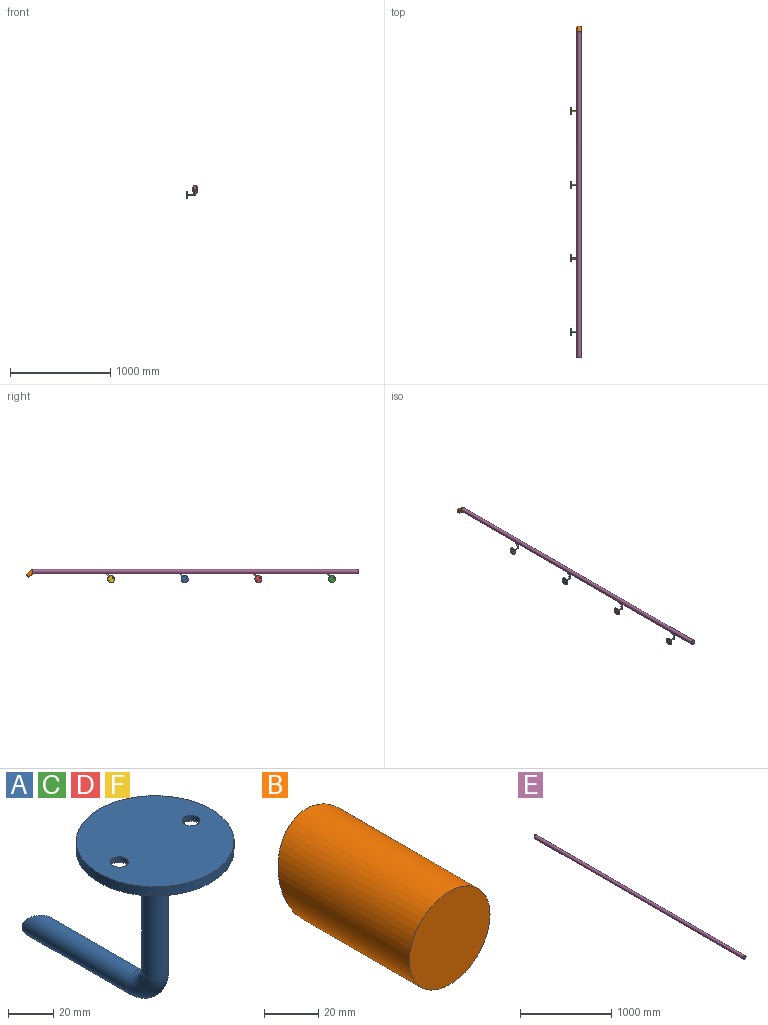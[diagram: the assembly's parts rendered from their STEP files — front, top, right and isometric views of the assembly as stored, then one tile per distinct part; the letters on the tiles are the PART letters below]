
ASSEMBLY  parts=6 mates=5
PART A: 11 faces, bbox 72.1x114.6x92.1 mm
  f0: cylinder r=6mm len=65.53mm, axis (0,-1,0), area 2289.2mm2, adj f1,f10
  f1: torus R=12mm, axis (-1,0,0), area 710.6mm2, adj f0,f2
  f2: cylinder r=6mm len=65.5mm, axis (0,0,1), area 2469.3mm2, adj f1,f5
  f3: cylinder r=35mm len=70mm, axis (0,0,-1), area 1099.6mm2, adj f4,f5
  f4: plane 70x70mm, normal (0,0,1), area 3747.9mm2, adj f3,f6,f7
  f5: plane 70x70mm, normal (0,0,-1), area 3469.9mm2, adj f2,f3,f8,f9
  f6: cylinder r=4mm len=8mm, axis (0,0,-1), area 62.8mm2, adj f4,f9
  f7: cylinder r=4mm len=8mm, axis (0,0,-1), area 62.8mm2, adj f4,f8
  f8: cone r=4mm half-angle=45deg, axis (0,0,-1), area 116.6mm2, adj f5,f7
  f9: cone r=4mm half-angle=45deg, axis (0,0,-1), area 116.6mm2, adj f5,f6
  f10: plane 14.08x14.08mm, normal (0.64,0.77,0), area 146.6mm2, adj f0
PART B: 5 faces, bbox 42.3x75x42.3 mm
  f0: cylinder r=18.5mm len=69.05mm, axis (0,1,0), area 7254.1mm2, adj f3,f4
  f1: cylinder r=21.15mm len=75mm, axis (0,1,0), area 8957.6mm2, adj f2,f4
  f2: plane 42.3x42.3mm, normal (0,-1,0), area 1405.3mm2, adj f1
  f3: plane 37x37mm, normal (0,1,0), area 1075.2mm2, adj f0
  f4: plane 42.3x42.3mm, normal (0,0.94,-0.34), area 350.7mm2, adj f0,f1
PART C: same geometry as A
PART D: same geometry as A
PART E: 8 faces, bbox 42.4x3250.1x42.4 mm
  f0: cylinder r=21.2mm len=3250.09mm, axis (0,1,0), area 392602mm2, adj f3,f4,f5,f6
  f1: cylinder r=18.95mm len=3240mm, axis (0,1,0), area 385342.4mm2, adj f2,f6,f7
  f2: plane 35x11.68mm, normal (0,-1,0), area 295.3mm2, adj f1,f6
  f3: plane 3230.09x12mm, normal (0,0,-1), area 38761.1mm2, adj f0,f5,f6
  f4: plane 42.4x42.4mm, normal (0,-1,0), area 1412mm2, adj f0
  f5: plane 12x0.87mm, normal (0,1,0), area 7mm2, adj f0,f3
  f6: plane 42.4x41.53mm, normal (0,0.94,-0.34), area 607.9mm2, adj f0,f1,f2,f3
  f7: plane 37.9x37.9mm, normal (0,1,0), area 1128.2mm2, adj f1
PART F: same geometry as A
PLACE A rot(axis=(0.39,-0.83,-0.39),100.5deg) t=(0,1774.81,-16.52)mm
PLACE B rot(axis=(0,0.34,0.94),180deg) t=(0,3236.53,4.83)mm
PLACE C rot(axis=(0.39,-0.83,-0.39),100.5deg) t=(0,308.15,-16.52)mm
PLACE D rot(axis=(0.39,-0.83,-0.39),100.5deg) t=(0,1041.48,-16.52)mm
PLACE E at identity
PLACE F rot(axis=(0.39,-0.83,-0.39),100.5deg) t=(0,2508.15,-16.52)mm
MATE fastened C.f10 <-> E.f3  axis (0,0,1) through (0,305,-20.33)mm
MATE fastened F.f10 <-> E.f3  axis (0,0,1) through (0,2505,-20.33)mm
MATE fastened A.f10 <-> E.f3  axis (0,0,1) through (0,1771.66,-20.33)mm
MATE fastened B.f4 <-> E.f6  axis (0,-0.94,0.34) through (0,3242.39,0)mm
MATE fastened D.f10 <-> E.f3  axis (0,0,1) through (0,1038.33,-20.33)mm
